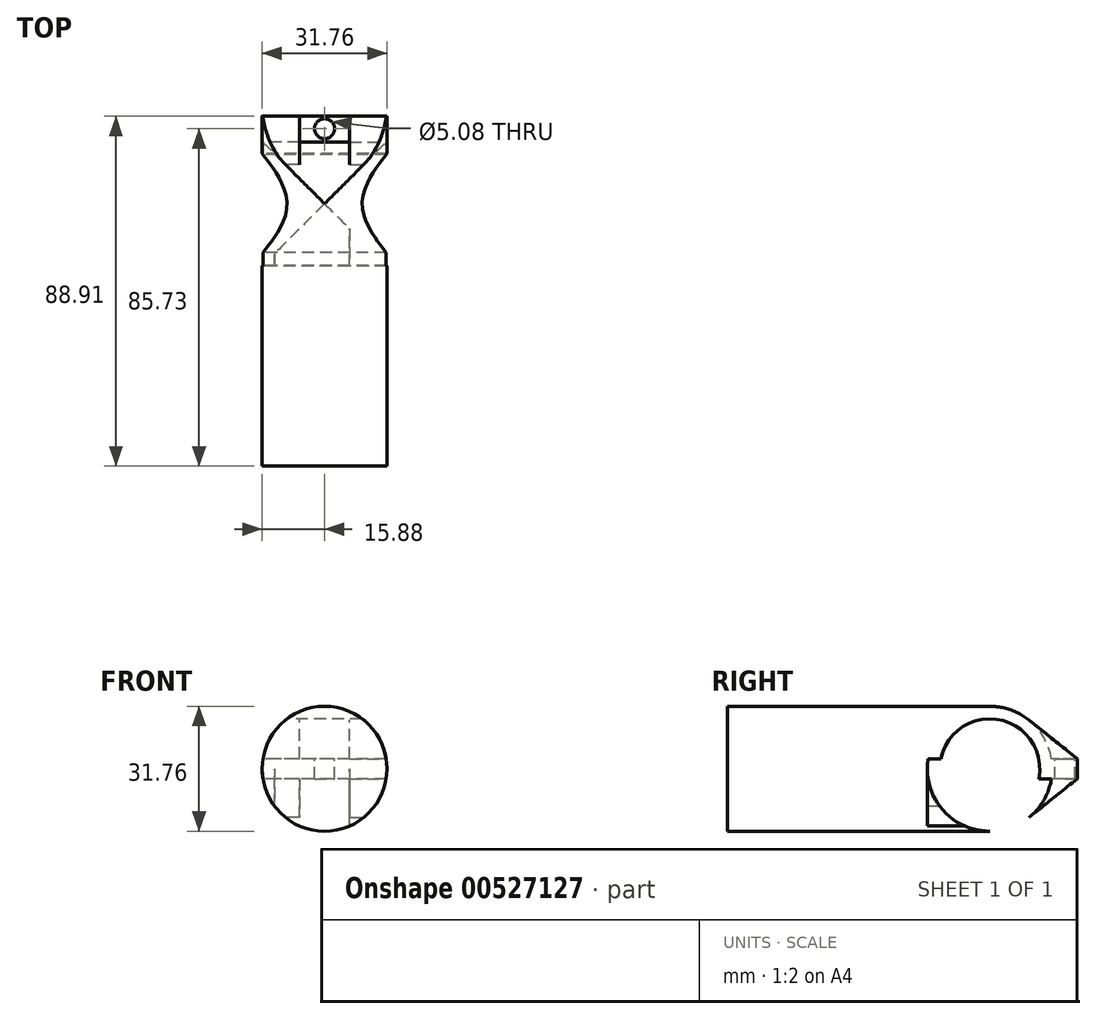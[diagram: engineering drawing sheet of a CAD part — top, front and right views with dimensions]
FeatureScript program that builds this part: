
annotation { "Feature Type Name" : "Feature", "Feature Type Description" : "" }
export const myFeature = defineFeature(function(context is Context, id is Id, definition is map)
    precondition{}
    {
        {
            var Q0;
            Q0=qCreatedBy(makeId("Right.planeOp"),FACE);
            var sketch = newSketch(context, id + "F0", { "sketchPlane" : qUnion([Q0])});
            skCircle(sketch, "E0", {"center": v(0, 0) * mm, "radius": 12.7 * mm});
            skCircle(sketch, "E1.0", {"center": v(0, 0) * mm, "radius": 15.88 * mm});
            skLineSegment(sketch, "E2.bottom", {"start": v(22.23, 2.54) * mm, "end": v(-22.22, 2.54) * mm});
            skLineSegment(sketch, "E2.top", {"start": v(22.23, -2.54) * mm, "end": v(-22.22, -2.54) * mm});
            skLineSegment(sketch, "E2.left", {"start": v(22.22, 2.54) * mm, "end": v(22.22, -2.54) * mm});
            skLineSegment(sketch, "E2.right", {"start": v(-22.23, 2.54) * mm, "end": v(-22.23, -2.54) * mm});
            skLineSegment(sketch, "E3", {"start": v(22.23, 2.54) * mm, "end": v(9.92, 12.4) * mm});
            skLineSegment(sketch, "E4", {"start": v(22.23, -2.54) * mm, "end": v(9.92, -12.4) * mm});
            skPoint(sketch, "E5.firstSnap0", {"position": v(-22.23, 0) * mm});
            skLineSegment(sketch, "E5.bottom", {"start": v(-15.88, 0) * mm, "end": v(-66.68, 0) * mm});
            skLineSegment(sketch, "E5.top", {"start": v(-15.88, 15.88) * mm, "end": v(-66.68, 15.87) * mm});
            skLineSegment(sketch, "E5.left", {"start": v(-15.88, 0) * mm, "end": v(-15.88, 15.88) * mm});
            skLineSegment(sketch, "E5.right", {"start": v(-66.68, 0) * mm, "end": v(-66.68, 15.87) * mm});
            skLineSegment(sketch, "E6", {"start": v(0, 15.88) * mm, "end": v(-15.88, 15.88) * mm});
            skLineSegment(sketch, "E7", {"start": v(0, -15.88) * mm, "end": v(-15.88, -15.88) * mm});
            skLineSegment(sketch, "E8", {"start": v(-15.88, -15.88) * mm, "end": v(-15.88, 0) * mm});
            skSolve(sketch);
        }
        {
            var Q0;
            {var subQ2=sQuery(id+"F0.wireOp",EDGE,"E2.bottom");var subQ6=sQuery(id+"F0.wireOp",EDGE,"E0");var subQ7=makeQuery(id+"F0.imprint","INTERSECT",VERTEX,{"disambiguationData":[OD(0.0)],"derivedFrom":[subQ6,subQ2]});Q0=makeQuery(id+"F0.imprint","IMPRINT",FACE,{"disambiguationData":[TD([[makeQuery(id+"F0.imprint","IMPRINT",EDGE,{"disambiguationData":[TD([[subQ7,1.0]])],"derivedFrom":subQ6}),-1.0]])]});}
            var Q1;
            {var subQ0=sQuery(id+"F0.wireOp",EDGE,"E6");Q1=makeQuery(id+"F0.imprint","IMPRINT",FACE,{"disambiguationData":[TD([[makeQuery(id+"F0.imprint","IMPRINT",EDGE,{"derivedFrom":subQ0}),1.0]])]});}
            var Q2;
            {var subQ0=sQuery(id+"F0.wireOp",EDGE,"E7");Q2=makeQuery(id+"F0.imprint","IMPRINT",FACE,{"disambiguationData":[TD([[makeQuery(id+"F0.imprint","IMPRINT",EDGE,{"derivedFrom":subQ0}),-1.0]])]});}
            var Q3;
            {var subQ2=sQuery(id+"F0.wireOp",EDGE,"E2.top");var subQ4=sQuery(id+"F0.wireOp",EDGE,"E0");var subQ5=makeQuery(id+"F0.imprint","INTERSECT",VERTEX,{"disambiguationData":[OD(0.0)],"derivedFrom":[subQ4,subQ2]});Q3=makeQuery(id+"F0.imprint","IMPRINT",FACE,{"disambiguationData":[TD([[makeQuery(id+"F0.imprint","IMPRINT",EDGE,{"disambiguationData":[TD([[subQ5,-1.0]])],"derivedFrom":subQ4}),-1.0]])]});}
            var Q4;
            {var subQ4=sQuery(id+"F0.wireOp",EDGE,"E2.bottom");var subQ6=sQuery(id+"F0.wireOp",EDGE,"E0");var subQ7=makeQuery(id+"F0.imprint","INTERSECT",VERTEX,{"disambiguationData":[OD(0.0)],"derivedFrom":[subQ6,subQ4]});Q4=makeQuery(id+"F0.imprint","IMPRINT",FACE,{"disambiguationData":[TD([[makeQuery(id+"F0.imprint","IMPRINT",EDGE,{"disambiguationData":[TD([[subQ7,-1.0]])],"derivedFrom":subQ6}),-1.0]])]});}
            var Q5;
            {var subQ0=sQuery(id+"F0.wireOp",EDGE,"E2.bottom");var subQ1=sQuery(id+"F0.wireOp",EDGE,"E0");var subQ2=makeQuery(id+"F0.imprint","INTERSECT",VERTEX,{"disambiguationData":[OD(1.0)],"derivedFrom":[subQ1,subQ0]});Q5=makeQuery(id+"F0.imprint","IMPRINT",FACE,{"disambiguationData":[TD([[makeQuery(id+"F0.imprint","IMPRINT",EDGE,{"disambiguationData":[TD([[subQ2,1.0]])],"derivedFrom":subQ1}),-1.0]])]});}
            var Q6;
            {var subQ5=sQuery(id+"F0.wireOp",EDGE,"E2.left");Q6=makeQuery(id+"F0.imprint","IMPRINT",FACE,{"disambiguationData":[TD([[makeQuery(id+"F0.imprint","IMPRINT",EDGE,{"derivedFrom":subQ5}),-1.0]])]});}
            var Q7;
            {var subQ1=sQuery(id+"F0.wireOp",EDGE,"E1.0");var subQ3=sQuery(id+"F0.wireOp",EDGE,"E2.bottom");var subQ4=makeQuery(id+"F0.imprint","INTERSECT",VERTEX,{"disambiguationData":[OD(1.0)],"derivedFrom":[subQ1,subQ3]});Q7=makeQuery(id+"F0.imprint","IMPRINT",FACE,{"disambiguationData":[TD([[makeQuery(id+"F0.imprint","IMPRINT",EDGE,{"disambiguationData":[TD([[subQ4,-1.0]])],"derivedFrom":subQ3}),1.0]])]});}
            var Q8;
            {var subQ0=sQuery(id+"F0.wireOp",EDGE,"E8");var subQ3=sQuery(id+"F0.wireOp",EDGE,"E2.top");var subQ5=makeQuery(id+"F0.imprint","INTERSECT",VERTEX,{"derivedFrom":[subQ3,subQ0]});Q8=makeQuery(id+"F0.imprint","IMPRINT",FACE,{"disambiguationData":[TD([[makeQuery(id+"F0.imprint","IMPRINT",EDGE,{"disambiguationData":[TD([[subQ5,1.0]])],"derivedFrom":subQ3}),-1.0]])]});}
            extrude(context, id + "F1", {"entities" : qUnion([Q0, Q1, Q2, Q3, Q4, Q5, Q6, Q7, Q8]), "depth" : 6.35 * mm, "offsetDistance" : 25.4 * mm});
        }
        {
            var Q0;
            {var subQ0=sQuery(id+"F0.wireOp",EDGE,"E3");Q0=makeQuery(id+"F0.imprint","IMPRINT",FACE,{"disambiguationData":[TD([[makeQuery(id+"F0.imprint","IMPRINT",EDGE,{"derivedFrom":subQ0}),1.0]])]});}
            var Q1;
            {var subQ0=sQuery(id+"F0.wireOp",EDGE,"E4");Q1=makeQuery(id+"F0.imprint","IMPRINT",FACE,{"disambiguationData":[TD([[makeQuery(id+"F0.imprint","IMPRINT",EDGE,{"derivedFrom":subQ0}),-1.0]])]});}
            var Q2;
            {var subQ2=sQuery(id+"F0.wireOp",EDGE,"E2.bottom");var subQ6=sQuery(id+"F0.wireOp",EDGE,"E0");var subQ7=makeQuery(id+"F0.imprint","INTERSECT",VERTEX,{"disambiguationData":[OD(0.0)],"derivedFrom":[subQ6,subQ2]});Q2=makeQuery(id+"F0.imprint","IMPRINT",FACE,{"disambiguationData":[TD([[makeQuery(id+"F0.imprint","IMPRINT",EDGE,{"disambiguationData":[TD([[subQ7,1.0]])],"derivedFrom":subQ6}),-1.0]])]});}
            var Q3;
            {var subQ0=sQuery(id+"F0.wireOp",EDGE,"E2.bottom");var subQ1=sQuery(id+"F0.wireOp",EDGE,"E0");var subQ2=makeQuery(id+"F0.imprint","INTERSECT",VERTEX,{"disambiguationData":[OD(1.0)],"derivedFrom":[subQ1,subQ0]});Q3=makeQuery(id+"F0.imprint","IMPRINT",FACE,{"disambiguationData":[TD([[makeQuery(id+"F0.imprint","IMPRINT",EDGE,{"disambiguationData":[TD([[subQ2,1.0]])],"derivedFrom":subQ1}),-1.0]])]});}
            var Q4;
            {var subQ5=sQuery(id+"F0.wireOp",EDGE,"E2.left");Q4=makeQuery(id+"F0.imprint","IMPRINT",FACE,{"disambiguationData":[TD([[makeQuery(id+"F0.imprint","IMPRINT",EDGE,{"derivedFrom":subQ5}),-1.0]])]});}
            var Q5;
            {var subQ2=sQuery(id+"F0.wireOp",EDGE,"E2.top");var subQ4=sQuery(id+"F0.wireOp",EDGE,"E0");var subQ5=makeQuery(id+"F0.imprint","INTERSECT",VERTEX,{"disambiguationData":[OD(0.0)],"derivedFrom":[subQ4,subQ2]});Q5=makeQuery(id+"F0.imprint","IMPRINT",FACE,{"disambiguationData":[TD([[makeQuery(id+"F0.imprint","IMPRINT",EDGE,{"disambiguationData":[TD([[subQ5,-1.0]])],"derivedFrom":subQ4}),-1.0]])]});}
            var Q6;
            {var subQ4=sQuery(id+"F0.wireOp",EDGE,"E2.bottom");var subQ6=sQuery(id+"F0.wireOp",EDGE,"E0");var subQ7=makeQuery(id+"F0.imprint","INTERSECT",VERTEX,{"disambiguationData":[OD(0.0)],"derivedFrom":[subQ6,subQ4]});Q6=makeQuery(id+"F0.imprint","IMPRINT",FACE,{"disambiguationData":[TD([[makeQuery(id+"F0.imprint","IMPRINT",EDGE,{"disambiguationData":[TD([[subQ7,-1.0]])],"derivedFrom":subQ6}),-1.0]])]});}
            var Q7;
            {var subQ0=sQuery(id+"F0.wireOp",EDGE,"E8");var subQ3=sQuery(id+"F0.wireOp",EDGE,"E2.top");var subQ5=makeQuery(id+"F0.imprint","INTERSECT",VERTEX,{"derivedFrom":[subQ3,subQ0]});Q7=makeQuery(id+"F0.imprint","IMPRINT",FACE,{"disambiguationData":[TD([[makeQuery(id+"F0.imprint","IMPRINT",EDGE,{"disambiguationData":[TD([[subQ5,1.0]])],"derivedFrom":subQ3}),-1.0]])]});}
            var Q8;
            {var subQ1=sQuery(id+"F0.wireOp",EDGE,"E1.0");var subQ3=sQuery(id+"F0.wireOp",EDGE,"E2.bottom");var subQ4=makeQuery(id+"F0.imprint","INTERSECT",VERTEX,{"disambiguationData":[OD(1.0)],"derivedFrom":[subQ1,subQ3]});Q8=makeQuery(id+"F0.imprint","IMPRINT",FACE,{"disambiguationData":[TD([[makeQuery(id+"F0.imprint","IMPRINT",EDGE,{"disambiguationData":[TD([[subQ4,-1.0]])],"derivedFrom":subQ3}),1.0]])]});}
            var Q9;
            {var subQ0=sQuery(id+"F0.wireOp",EDGE,"E6");Q9=makeQuery(id+"F0.imprint","IMPRINT",FACE,{"disambiguationData":[TD([[makeQuery(id+"F0.imprint","IMPRINT",EDGE,{"derivedFrom":subQ0}),1.0]])]});}
            var Q10;
            {var subQ0=sQuery(id+"F0.wireOp",EDGE,"E7");Q10=makeQuery(id+"F0.imprint","IMPRINT",FACE,{"disambiguationData":[TD([[makeQuery(id+"F0.imprint","IMPRINT",EDGE,{"derivedFrom":subQ0}),-1.0]])]});}
            extrude(context, id + "F2", {"entities" : qUnion([Q0, Q1, Q2, Q3, Q4, Q5, Q6, Q7, Q8, Q9, Q10]), "oppositeDirection" : true, "depth" : 12.7 * mm, "offsetDistance" : 25.4 * mm});
        }
        {
            var Q0;
            Q0=makeQuery(id+"F2.opExtrude","SWEPT_BODY",BODY,{"disambiguationData":[OSD([sQuery(id+"F0.wireOp",EDGE,"E0"),sQuery(id+"F0.wireOp",EDGE,"E1.0"),sQuery(id+"F0.wireOp",EDGE,"E2.left"),sQuery(id+"F0.wireOp",EDGE,"E3"),sQuery(id+"F0.wireOp",EDGE,"E4"),sQuery(id+"F0.wireOp",EDGE,"E5.left"),sQuery(id+"F0.wireOp",EDGE,"E6"),sQuery(id+"F0.wireOp",EDGE,"E7"),sQuery(id+"F0.wireOp",EDGE,"E8")])]});
            transform(context, id + "F3", {"entities" : qUnion([Q0]), "transformType" : TransformType.TRANSLATION_3D, "dx" : 19.05 * mm, "dy" : 0 * mm, "dz" : 0 * mm, "makeCopy" : false});
        }
        {
            var Q0;
            Q0=makeQuery(id+"F1.opExtrude","SWEPT_BODY",BODY,{"disambiguationData":[OSD([sQuery(id+"F0.wireOp",EDGE,"E0"),sQuery(id+"F0.wireOp",EDGE,"E1.0"),sQuery(id+"F0.wireOp",EDGE,"E2.bottom"),sQuery(id+"F0.wireOp",EDGE,"E2.top"),sQuery(id+"F0.wireOp",EDGE,"E2.left"),sQuery(id+"F0.wireOp",EDGE,"E5.left"),sQuery(id+"F0.wireOp",EDGE,"E6"),sQuery(id+"F0.wireOp",EDGE,"E7"),sQuery(id+"F0.wireOp",EDGE,"E8")])]});
            var Q1;
            Q1=makeQuery(id+"F2.opExtrude","SWEPT_BODY",BODY,{"disambiguationData":[OSD([sQuery(id+"F0.wireOp",EDGE,"E0"),sQuery(id+"F0.wireOp",EDGE,"E1.0"),sQuery(id+"F0.wireOp",EDGE,"E2.left"),sQuery(id+"F0.wireOp",EDGE,"E3"),sQuery(id+"F0.wireOp",EDGE,"E4"),sQuery(id+"F0.wireOp",EDGE,"E5.left"),sQuery(id+"F0.wireOp",EDGE,"E6"),sQuery(id+"F0.wireOp",EDGE,"E7"),sQuery(id+"F0.wireOp",EDGE,"E8")])]});
            booleanBodies(context, id + "F4", {"operationType" : BooleanOperationType.UNION, "tools" : qUnion([Q0, Q1])});
        }
        {
            var Q0;
            Q0=makeQuery(id+"F1.opExtrude","SWEPT_BODY",BODY,{"disambiguationData":[OSD([sQuery(id+"F0.wireOp",EDGE,"E0"),sQuery(id+"F0.wireOp",EDGE,"E1.0"),sQuery(id+"F0.wireOp",EDGE,"E2.bottom"),sQuery(id+"F0.wireOp",EDGE,"E2.top"),sQuery(id+"F0.wireOp",EDGE,"E2.left"),sQuery(id+"F0.wireOp",EDGE,"E5.left"),sQuery(id+"F0.wireOp",EDGE,"E6"),sQuery(id+"F0.wireOp",EDGE,"E7"),sQuery(id+"F0.wireOp",EDGE,"E8")])]});
            var Q1;
            Q1=qCreatedBy(makeId("Right.planeOp"),FACE);
            mirror(context, id + "F5", {"operationType" : NewBodyOperationType.ADD, "entities" : qUnion([Q0]), "mirrorPlane" : qUnion([Q1])});
        }
        {
            var Q0;
            {var subQ0=makeQuery(id+"F1.opExtrude","SWEPT_FACE",FACE,{"disambiguationData":[OSD([sQuery(id+"F0.wireOp",EDGE,"E2.bottom")])]});Q0=makeQuery(id+"F5.boolean.opBoolean","MERGE",FACE,{"derivedFrom":[subQ0,makeQuery(id+"F5.opPattern","COPY",FACE,{"derivedFrom":subQ0,"instanceName":"1"})]});}
            var sketch = newSketch(context, id + "F6", { "sketchPlane" : qUnion([Q0])});
            skCircle(sketch, "E9", {"center": v(0, 19.05) * mm, "radius": 2.54 * mm});
            skPoint(sketch, "E9.centerSnap0", {"position": v(0, 15.67) * mm});
            skSolve(sketch);
        }
        {
            var Q0;
            Q0=makeQuery(id+"F6.imprint","IMPRINT",FACE,{"disambiguationData":[TD([[makeQuery(id+"F6.imprint","IMPRINT",EDGE,{"derivedFrom":sQuery(id+"F6.wireOp",EDGE,"E9")}),1.0]])]});
            extrude(context, id + "F7", {"entities" : qUnion([Q0]), "operationType" : NewBodyOperationType.REMOVE, "oppositeDirection" : true, "depth" : 25.4 * mm, "offsetDistance" : 25.4 * mm});
        }
        {
            var Q0;
            {var subQ0=sQuery(id+"F0.wireOp",EDGE,"E5.top");Q0=makeQuery(id+"F0.imprint","IMPRINT",FACE,{"disambiguationData":[TD([[makeQuery(id+"F0.imprint","IMPRINT",EDGE,{"derivedFrom":subQ0}),1.0]])]});}
            var Q1;
            {var subQ0=sQuery(id+"F0.wireOp",EDGE,"E2.right");var subQ1=sQuery(id+"F0.wireOp",EDGE,"E2.bottom");var subQ2=makeQuery(id+"F0.imprint","INTERSECT",VERTEX,{"derivedFrom":[subQ1,subQ0]});Q1=makeQuery(id+"F0.imprint","IMPRINT",FACE,{"disambiguationData":[TD([[makeQuery(id+"F0.imprint","IMPRINT",EDGE,{"disambiguationData":[TD([[subQ2,1.0]])],"derivedFrom":subQ1}),1.0]])]});}
            var Q2;
            Q2=sQuery(id+"F0.wireOp",EDGE,"E5.bottom");
            revolve(context, id + "F8", {"operationType" : NewBodyOperationType.ADD, "entities" : qUnion([Q0, Q1]), "axis" : qUnion([Q2]), "revolveType" : RevolveType.FULL});
        }
        {
            var Q0;
            Q0=makeQuery(id+"F8.opRevolve","SWEPT_FACE",FACE,{"disambiguationData":[OSD([sQuery(id+"F0.wireOp",EDGE,"E5.right")])]});
            var sketch = newSketch(context, id + "F9", { "sketchPlane" : qUnion([Q0])});
            skCircle(sketch, "E10.0", {"center": v(0, 0) * mm, "radius": 28.57 * mm});
            skSolve(sketch);
        }
        {
            var Q0;
            Q0=makeQuery(id+"F9.imprint","IMPRINT",FACE,{"disambiguationData":[TD([[makeQuery(id+"F9.imprint","IMPRINT",EDGE,{"derivedFrom":sQuery(id+"F9.wireOp",EDGE,"E10.0")}),1.0]])]});
            extrude(context, id + "F10", {"entities" : qUnion([Q0]), "operationType" : NewBodyOperationType.REMOVE, "oppositeDirection" : true, "depth" : 254 * mm, "offsetDistance" : 25.4 * mm});
        }
    });
